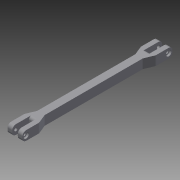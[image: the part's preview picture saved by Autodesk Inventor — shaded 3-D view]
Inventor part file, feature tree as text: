
AUTODESK INVENTOR PART (.ipt)
format: ipt  version: 2015 (Build 190159000, 159)  size: 167,424 bytes
history: native  units: mm
features: sketch x4, fillet x4, extrude x2, plane x2, mirror x2, loft x1, hole x1, other x1
ambient origin geometry x8: Origin, YZ Plane, XZ Plane, XY Plane, X Axis, Y Axis, Z Axis, Center Point
bodies: Solid1 (feature_tree)
feature tree (17):
  extrude  "Extrusion1"  Depth=10.0mm
  sketch  "Sketch2"  dims[d2=126.0mm d3=0.0mm d4=5.0mm]
  sketch  "Sketch3"  dims[d5=5.0mm d6=3.05mm d7=3.05mm d8=10.0mm]
  extrude  "Extrusion3"  Depth=5.0mm
  loft  "Loft2"
  plane  "Work Plane2"
  fillet  "Fillet4"  Radius=3.05mm
  fillet  "Fillet5"  Radius=10.0mm
  hole  "Hole1"  [1 undecoded]
  mirror  "Mirror2"
  plane  "Work Plane3"
  mirror  "Mirror3"
  fillet  "Fillet6"  [1 undecoded]
  fillet  "Fillet7"  Radius=4.0mm
  sketch  "Sketch1"  dims[d0=8.0mm d1=10.0mm]
  other  "Edges1"
  sketch  "Sketch5"  dims[d18=18.0mm d19=0.0mm d20=0.0mm d21=90.0deg d22=0.0mm d23=90.0deg d24=4.0mm d25=4.0mm d26=3.3mm d27=6.0mm d28=6.0mm d29=2.0mm d30=90.0deg d31=8.0mm d32=20.594885mm d42=3.0mm d43=3.0mm]
note: 2 required parameter values undecoded (feature->parameter linkage not recoverable at this tier; creation-order binding heuristic only, values carry confidence <= 0.55)
